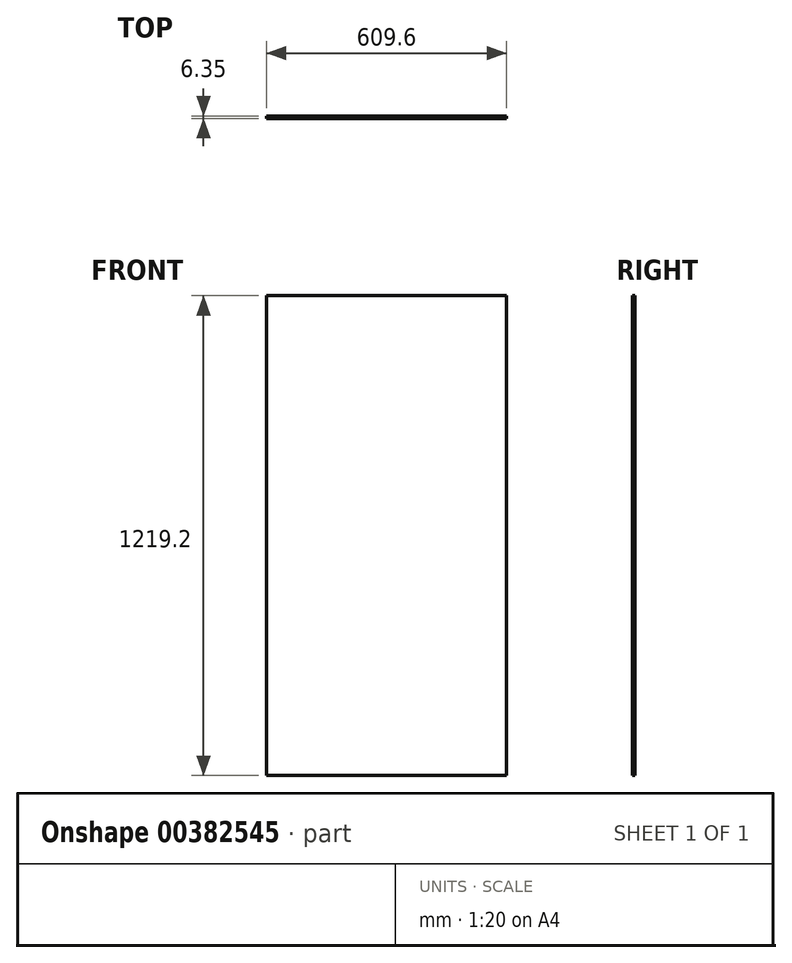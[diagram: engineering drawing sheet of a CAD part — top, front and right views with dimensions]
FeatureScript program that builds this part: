
annotation { "Feature Type Name" : "Feature", "Feature Type Description" : "" }
export const myFeature = defineFeature(function(context is Context, id is Id, definition is map)
    precondition{}
    {
        {
            var Q0;
            Q0=qCreatedBy(makeId("Front.planeOp"),FACE);
            var sketch = newSketch(context, id + "F0", { "sketchPlane" : qUnion([Q0])});
            skLineSegment(sketch, "E0.bottom", {"start": v(304.8, 609.6) * mm, "end": v(-304.8, 609.6) * mm});
            skLineSegment(sketch, "E0.top", {"start": v(304.8, -609.6) * mm, "end": v(-304.8, -609.6) * mm});
            skLineSegment(sketch, "E0.left", {"start": v(304.8, 609.6) * mm, "end": v(304.8, -609.6) * mm});
            skLineSegment(sketch, "E0.right", {"start": v(-304.8, 609.6) * mm, "end": v(-304.8, -609.6) * mm});
            skPoint(sketch, "E0.middle", {"position": v(0, 0) * mm});
            skSolve(sketch);
        }
        {
            var Q0;
            Q0=makeQuery(id+"F0.imprint","IMPRINT",FACE,{"disambiguationData":[TD([[makeQuery(id+"F0.imprint","IMPRINT",EDGE,{"derivedFrom":sQuery(id+"F0.wireOp",EDGE,"E0.bottom")}),1.0]])]});
            extrude(context, id + "F1", {"entities" : qUnion([Q0]), "depth" : 6.35 * mm});
        }
    });
